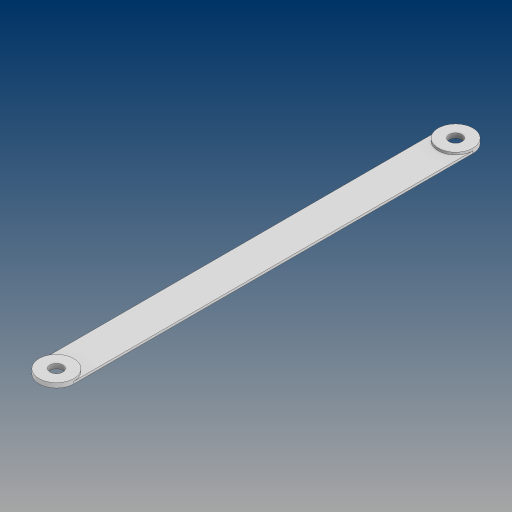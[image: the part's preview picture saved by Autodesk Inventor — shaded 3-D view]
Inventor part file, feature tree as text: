
AUTODESK INVENTOR PART (.ipt)
format: ipt  version: 2023 (Build 270158000, 158)  size: 113,664 bytes
history: native  units: mm
features: extrude x2, sketch x1
ambient origin geometry x8: Origin, YZ Plane, XZ Plane, XY Plane, X Axis, Y Axis, Z Axis, Center Point
bodies: Solid1 (feature_tree)
feature tree (3):
  sketch  "Sketch1"  dims[d0=157.681217mm d1=90.0deg d2=7.5mm d3=15.0mm d4=15.0mm d5=5.5mm d6=5.5mm d7=1.0mm d8=0.0mm d9=2.0mm d10=0.0mm d11=15.0mm d12=15.0mm d13=5.5mm d14=5.5mm]
  extrude  "Extrusion1"  TaperAngle=90.0deg  [1 undecoded]
  extrude  "Extrusion2"  Depth=7.5mm
note: 1 required parameter value undecoded (feature->parameter linkage not recoverable at this tier; creation-order binding heuristic only, values carry confidence <= 0.55)
